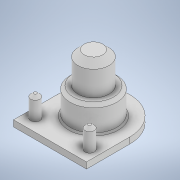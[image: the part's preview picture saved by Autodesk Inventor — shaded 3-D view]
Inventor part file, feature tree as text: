
AUTODESK INVENTOR PART (.ipt)
format: ipt  version: 2021 (Build 250183000, 183)  size: 160,768 bytes
history: native  units: mm
features: extrude x5, chamfer x5, sketch x5, other x1
ambient origin geometry x8: Origin, YZ Plane, XZ Plane, XY Plane, X Axis, Y Axis, Z Axis, Center Point
bodies: Body1 (feature_tree)
feature tree (16):
  other  "Sólido1"
  extrude  "Extrusión1"  Depth=10.0mm TaperAngle=0.0deg
  extrude  "Extrusión2"  Depth=3.5mm
  extrude  "Extrusión3"  Depth=10.0mm
  extrude  "Extrusión4"  Depth=0.5mm TaperAngle=45.0deg
  extrude  "Extrusión5"  Depth=1.0mm TaperAngle=45.0deg
  chamfer  "Chaflán1"  Distance=1.0mm Angle=45.0deg
  chamfer  "Chaflán2"  Distance=1.0mm Angle=45.0deg
  chamfer  "Chaflán3"  [1 undecoded]
  chamfer  "Chaflán4"  [1 undecoded]
  chamfer  "Chaflán5"  [1 undecoded]
  sketch  "Boceto1"  dims[d10=3.0mm d11=0.0mm d12=10.0mm d13=0.0mm]
  sketch  "Boceto2"  dims[d14=3.5mm d15=0.0mm d16=15.0mm]
  sketch  "Boceto3"  dims[d17=8.0mm d18=0.0mm d19=10.0mm]
  sketch  "Boceto4"  dims[d20=10.0mm d21=0.0mm d22=0.5mm d23=2.0mm d24=45.0deg]
  sketch  "Boceto5"  dims[d25=1.0mm d26=2.0mm d27=45.0deg d28=2.0mm d29=2.0mm d30=45.0deg d31=1.0mm d32=2.0mm d33=45.0deg d34=1.0mm d35=2.0mm d36=45.0deg]
note: 3 required parameter values undecoded (feature->parameter linkage not recoverable at this tier; creation-order binding heuristic only, values carry confidence <= 0.55)
